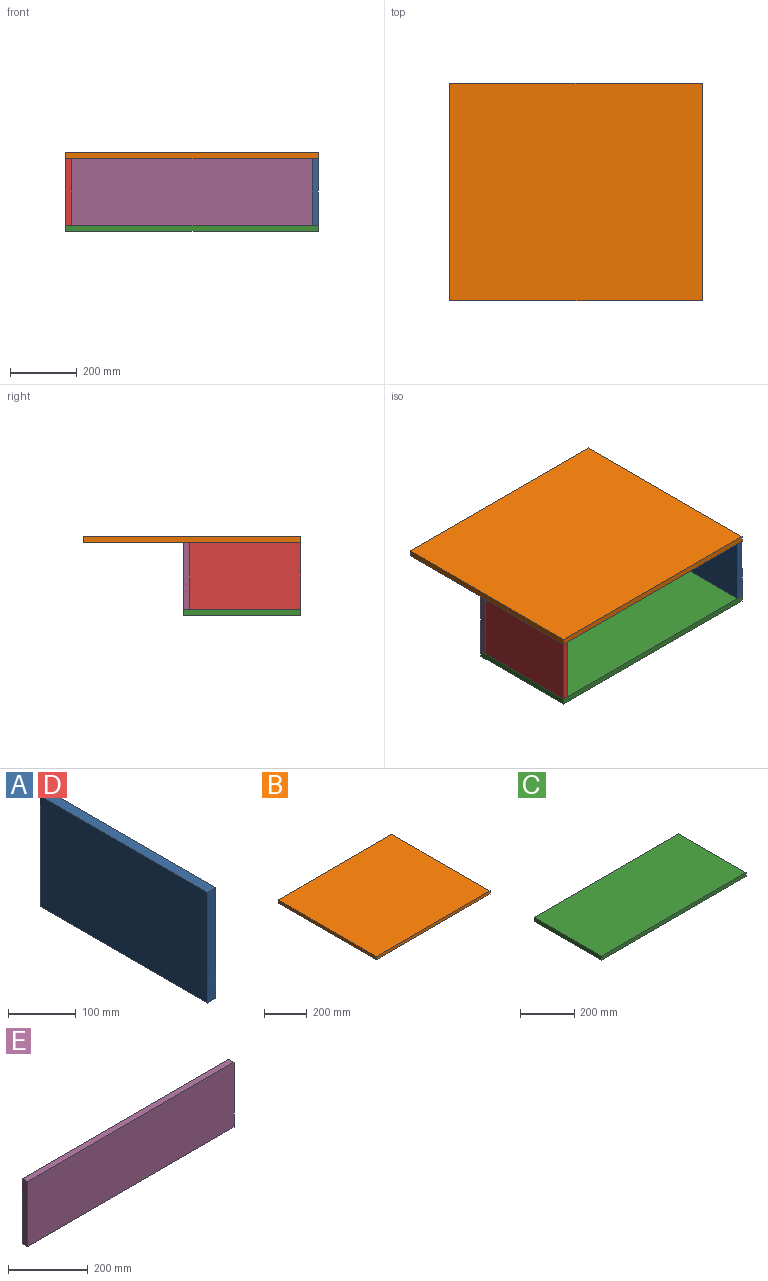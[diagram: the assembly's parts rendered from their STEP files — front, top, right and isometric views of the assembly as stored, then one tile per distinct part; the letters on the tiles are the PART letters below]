
ASSEMBLY  parts=5 mates=4
PART A: 6 faces, bbox 18x350x200 mm
  f0: plane 350x18mm, normal (0,0,-1), area 6300mm2, adj f1,f3,f4,f5
  f1: plane 200x18mm, normal (0,1,0), area 3600mm2, adj f0,f2,f4,f5
  f2: plane 350x18mm, normal (0,0,1), area 6300mm2, adj f1,f3,f4,f5
  f3: plane 200x18mm, normal (0,-1,0), area 3600mm2, adj f0,f2,f4,f5
  f4: plane 350x200mm, normal (1,0,0), area 70000mm2, adj f0,f1,f2,f3
  f5: plane 350x200mm, normal (-1,0,0), area 70000mm2, adj f0,f1,f2,f3
PART B: 6 faces, bbox 754x650x18 mm
  f0: plane 754x18mm, normal (0,-1,0), area 13572mm2, adj f1,f3,f4,f5
  f1: plane 650x18mm, normal (1,0,0), area 11700mm2, adj f0,f2,f4,f5
  f2: plane 754x18mm, normal (0,1,0), area 13572mm2, adj f1,f3,f4,f5
  f3: plane 650x18mm, normal (-1,0,0), area 11700mm2, adj f0,f2,f4,f5
  f4: plane 754x650mm, normal (0,0,1), area 490100mm2, adj f0,f1,f2,f3
  f5: plane 754x650mm, normal (0,0,-1), area 490100mm2, adj f0,f1,f2,f3
PART C: 6 faces, bbox 754x350x18 mm
  f0: plane 754x18mm, normal (0,-1,0), area 13572mm2, adj f1,f3,f4,f5
  f1: plane 350x18mm, normal (1,0,0), area 6300mm2, adj f0,f2,f4,f5
  f2: plane 754x18mm, normal (0,1,0), area 13572mm2, adj f1,f3,f4,f5
  f3: plane 350x18mm, normal (-1,0,0), area 6300mm2, adj f0,f2,f4,f5
  f4: plane 754x350mm, normal (0,0,1), area 263900mm2, adj f0,f1,f2,f3
  f5: plane 754x350mm, normal (0,0,-1), area 263900mm2, adj f0,f1,f2,f3
PART D: same geometry as A
PART E: 6 faces, bbox 736x18x200 mm
  f0: plane 736x18mm, normal (0,0,-1), area 13248mm2, adj f1,f3,f4,f5
  f1: plane 200x18mm, normal (1,0,0), area 3600mm2, adj f0,f2,f4,f5
  f2: plane 736x18mm, normal (0,0,1), area 13248mm2, adj f1,f3,f4,f5
  f3: plane 200x18mm, normal (-1,0,0), area 3600mm2, adj f0,f2,f4,f5
  f4: plane 736x200mm, normal (0,-1,0), area 147200mm2, adj f0,f1,f2,f3
  f5: plane 736x200mm, normal (0,1,0), area 147200mm2, adj f0,f1,f2,f3
PLACE A t=(343.01,263.32,15.83)mm
PLACE B t=(-24.99,413.32,124.83)mm
PLACE C t=(-24.99,263.32,-93.17)mm
PLACE D t=(-392.99,263.32,15.83)mm
PLACE E t=(-33.99,429.32,15.83)mm
MATE fastened E.f0 <-> A.f0  axis (0,0,1) through (334.01,438.32,-84.17)mm
MATE fastened A.f3 <-> C.f0  axis (0,1,0) through (352.01,88.32,-84.17)mm
MATE fastened A.f3 <-> B.f0  axis (0,1,0) through (352.01,88.32,115.83)mm
MATE fastened B.f0 <-> D.f3  axis (0,1,0) through (-401.99,88.32,115.83)mm
